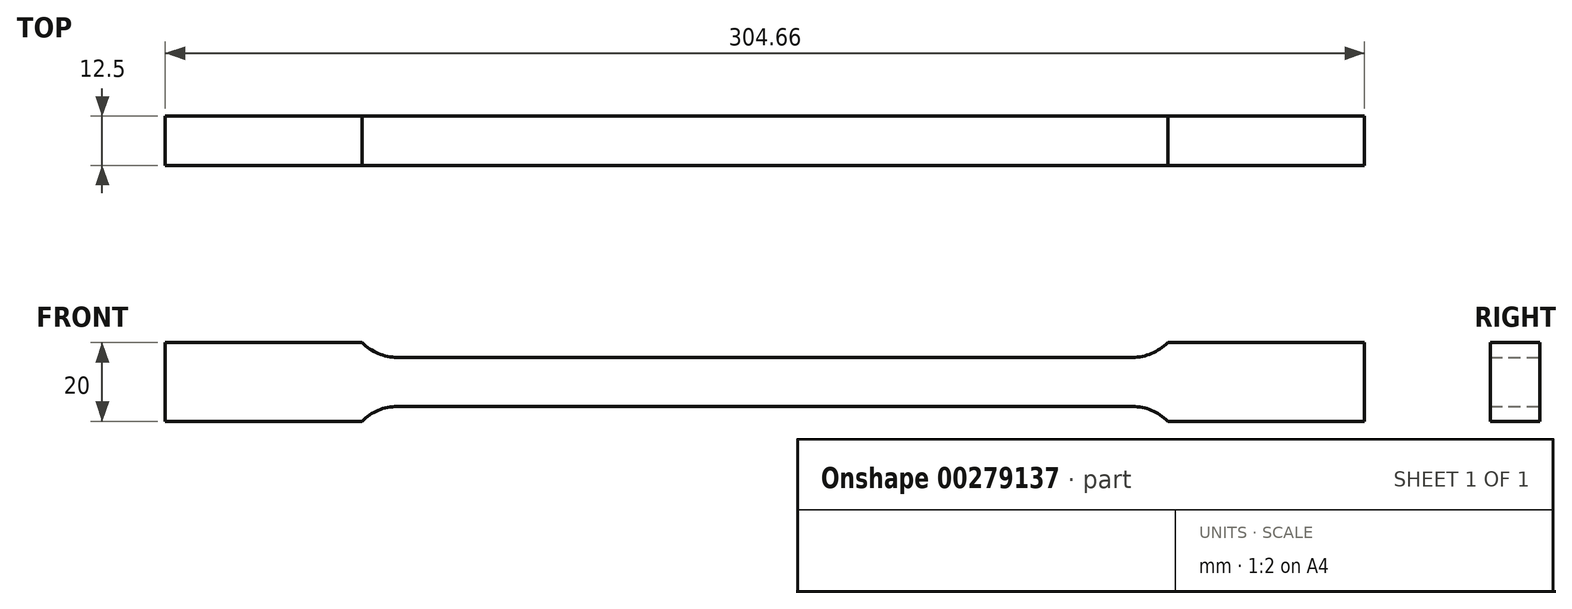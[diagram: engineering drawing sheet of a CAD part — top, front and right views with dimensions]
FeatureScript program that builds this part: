
annotation { "Feature Type Name" : "Feature", "Feature Type Description" : "" }
export const myFeature = defineFeature(function(context is Context, id is Id, definition is map)
    precondition{}
    {
        {
            var Q0;
            Q0=qCreatedBy(makeId("Front.planeOp"),FACE);
            var sketch = newSketch(context, id + "F0", { "sketchPlane" : qUnion([Q0])});
            skLineSegment(sketch, "E0", {"start": v(0, 6.25) * mm, "end": v(93.4, 6.25) * mm});
            skArc(sketch, "E1", {"start": v(93.4, 6.25) * mm, "mid": v(98.24, 7.23) * mm, "end": v(102.33, 10) * mm});
            skLineSegment(sketch, "E2", {"start": v(102.33, 10) * mm, "end": v(152.33, 10) * mm});
            skLineSegment(sketch, "E3", {"start": v(152.33, 10) * mm, "end": v(152.33, 0) * mm});
            skLineSegment(sketch, "E4.MirrorCS", {"start": v(152.33, -10) * mm, "end": v(152.33, 0) * mm});
            skLineSegment(sketch, "E5.MirrorCS", {"start": v(102.33, -10) * mm, "end": v(152.33, -10) * mm});
            skLineSegment(sketch, "E6.MirrorCS", {"start": v(0, -6.25) * mm, "end": v(93.4, -6.25) * mm});
            skArc(sketch, "E7.MirrorCS", {"start": v(93.4, -6.25) * mm, "mid": v(98.24, -7.23) * mm, "end": v(102.33, -10) * mm});
            skLineSegment(sketch, "E8.MirrorCS", {"start": v(-152.33, 10) * mm, "end": v(-152.33, 0) * mm});
            skLineSegment(sketch, "E9.MirrorCS", {"start": v(-102.33, 10) * mm, "end": v(-152.33, 10) * mm});
            skArc(sketch, "E10.MirrorCS", {"start": v(-93.4, 6.25) * mm, "mid": v(-98.24, 7.23) * mm, "end": v(-102.33, 10) * mm});
            skLineSegment(sketch, "E11.MirrorCS", {"start": v(0, -6.25) * mm, "end": v(-93.4, -6.25) * mm});
            skLineSegment(sketch, "E12.MirrorCS", {"start": v(-102.33, -10) * mm, "end": v(-152.33, -10) * mm});
            skLineSegment(sketch, "E13.MirrorCS", {"start": v(-152.33, -10) * mm, "end": v(-152.33, 0) * mm});
            skLineSegment(sketch, "E14.MirrorCS", {"start": v(0, 6.25) * mm, "end": v(-93.4, 6.25) * mm});
            skArc(sketch, "E15.MirrorCS", {"start": v(-93.4, -6.25) * mm, "mid": v(-98.24, -7.23) * mm, "end": v(-102.33, -10) * mm});
            skSolve(sketch);
        }
        {
            var Q0;
            Q0 = qSketchRegion(id + "F0", true);
            extrude(context, id + "F1", {"entities" : qUnion([Q0]), "endBound" : BoundingType.SYMMETRIC, "depth" : 12.5 * mm});
        }
    });
